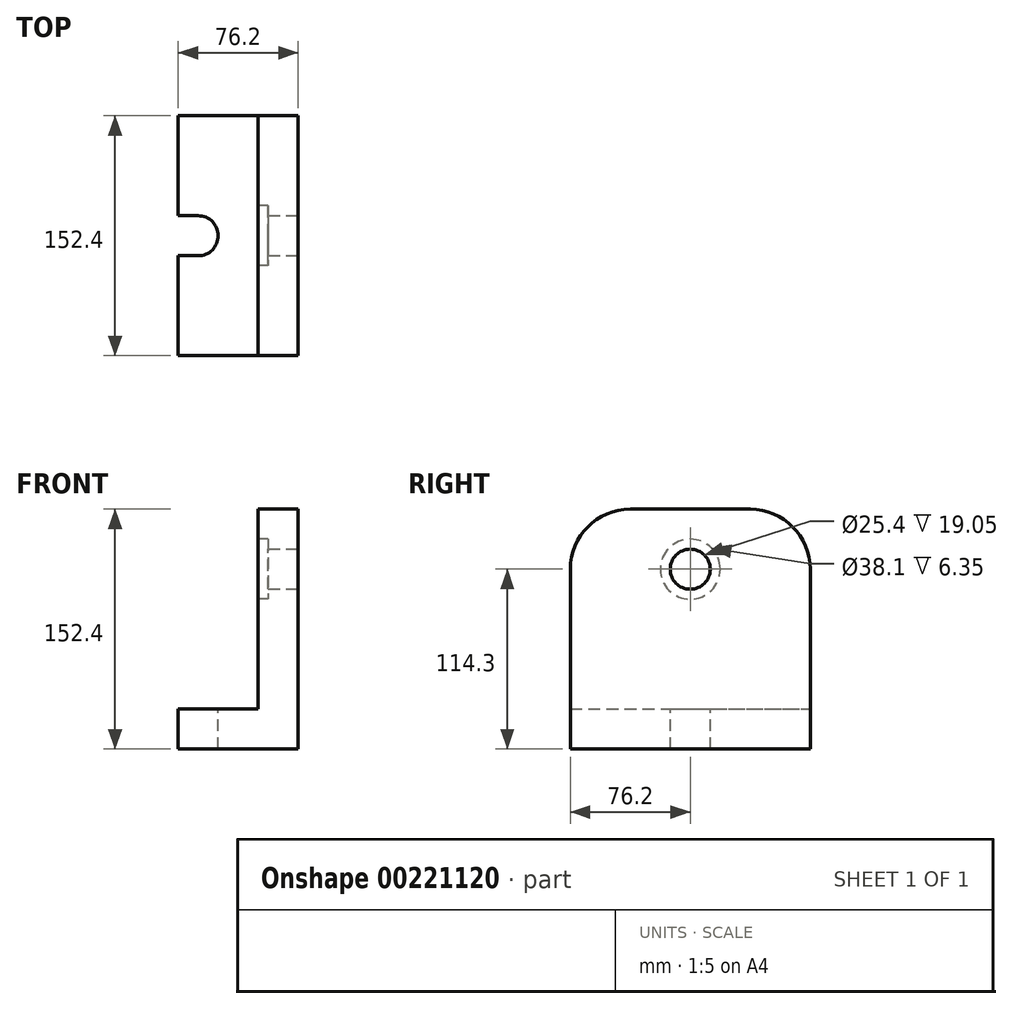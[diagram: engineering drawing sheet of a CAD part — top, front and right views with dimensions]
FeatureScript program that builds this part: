
annotation { "Feature Type Name" : "Feature", "Feature Type Description" : "" }
export const myFeature = defineFeature(function(context is Context, id is Id, definition is map)
    precondition{}
    {
        {
            var Q0;
            Q0=qCreatedBy(makeId("Front.planeOp"),FACE);
            var sketch = newSketch(context, id + "F0", { "sketchPlane" : qUnion([Q0])});
            skLineSegment(sketch, "E0", {"start": v(0, 0) * mm, "end": v(0, 152.4) * mm});
            skLineSegment(sketch, "E1", {"start": v(0, 152.4) * mm, "end": v(-25.4, 152.4) * mm});
            skLineSegment(sketch, "E2", {"start": v(-25.4, 152.4) * mm, "end": v(-25.4, 25.4) * mm});
            skLineSegment(sketch, "E3", {"start": v(-25.4, 25.4) * mm, "end": v(-76.2, 25.4) * mm});
            skLineSegment(sketch, "E4", {"start": v(-76.2, 25.4) * mm, "end": v(-76.2, 0) * mm});
            skLineSegment(sketch, "E5", {"start": v(-76.2, 0) * mm, "end": v(0, 0) * mm});
            skSolve(sketch);
        }
        {
            var Q0;
            Q0=makeQuery(id+"F0.imprint","IMPRINT",FACE,{"disambiguationData":[TD([[makeQuery(id+"F0.imprint","IMPRINT",EDGE,{"derivedFrom":sQuery(id+"F0.wireOp",EDGE,"E0")}),1.0]])]});
            extrude(context, id + "F1", {"entities" : qUnion([Q0]), "endBound" : BoundingType.SYMMETRIC, "depth" : 152.4 * mm});
        }
        {
            var Q0;
            Q0=makeQuery(id+"F1.opExtrude","SWEPT_FACE",FACE,{"disambiguationData":[OSD([sQuery(id+"F0.wireOp",EDGE,"E0")])]});
            var sketch = newSketch(context, id + "F2", { "sketchPlane" : qUnion([Q0])});
            skCircle(sketch, "E6", {"center": v(0, 114.3) * mm, "radius": 12.7 * mm});
            skSolve(sketch);
        }
        {
            var Q0;
            Q0=makeQuery(id+"F2.imprint","IMPRINT",FACE,{"disambiguationData":[TD([[makeQuery(id+"F2.imprint","IMPRINT",EDGE,{"derivedFrom":sQuery(id+"F2.wireOp",EDGE,"E6")}),1.0]])]});
            extrude(context, id + "F3", {"entities" : qUnion([Q0]), "operationType" : NewBodyOperationType.REMOVE, "endBound" : BoundingType.THROUGH_ALL, "oppositeDirection" : true, "depth" : 25.4 * mm});
        }
        {
            var Q0;
            Q0=makeQuery(id+"F1.opExtrude","SWEPT_FACE",FACE,{"disambiguationData":[OSD([sQuery(id+"F0.wireOp",EDGE,"E3")])]});
            var sketch = newSketch(context, id + "F4", { "sketchPlane" : qUnion([Q0])});
            skPoint(sketch, "E7.endSnap0", {"position": v(-76.2, 0) * mm});
            skPoint(sketch, "E8.positionSnap0", {"position": v(-50.8, 76.2) * mm});
            skLineSegment(sketch, "E9", {"start": v(-76.2, 0) * mm, "end": v(-63.5, 0) * mm});
            skLineSegment(sketch, "E10", {"start": v(-63.5, 12.7) * mm, "end": v(-76.2, 12.7) * mm});
            skLineSegment(sketch, "E11", {"start": v(-63.5, -12.7) * mm, "end": v(-76.2, -12.7) * mm});
            skArc(sketch, "E12", {"start": v(-63.5, -12.7) * mm, "mid": v(-50.8, 0) * mm, "end": v(-63.5, 12.7) * mm});
            skSolve(sketch);
        }
        {
            var Q0;
            {var subQ2=sQuery(id+"F4.wireOp",EDGE,"E10");Q0=makeQuery(id+"F4.imprint","IMPRINT",FACE,{"disambiguationData":[TD([[makeQuery(id+"F4.imprint","IMPRINT",EDGE,{"derivedFrom":subQ2}),1.0]])]});}
            extrude(context, id + "F5", {"entities" : qUnion([Q0]), "operationType" : NewBodyOperationType.REMOVE, "endBound" : BoundingType.THROUGH_ALL, "oppositeDirection" : true, "depth" : 25.4 * mm});
        }
        {
            var Q0;
            Q0=makeQuery(id+"F1.opExtrude","SWEPT_FACE",FACE,{"disambiguationData":[OSD([sQuery(id+"F0.wireOp",EDGE,"E2")])]});
            var sketch = newSketch(context, id + "F6", { "sketchPlane" : qUnion([Q0])});
            skCircle(sketch, "E13", {"center": v(0, 114.3) * mm, "radius": 19.05 * mm});
            skSolve(sketch);
        }
        {
            var Q0;
            Q0=makeQuery(id+"F6.imprint","IMPRINT",FACE,{"disambiguationData":[TD([[makeQuery(id+"F6.imprint","IMPRINT",EDGE,{"derivedFrom":sQuery(id+"F6.wireOp",EDGE,"E13")}),1.0]])]});
            var Q1;
            Q1=sQuery(id+"F6.wireOp",EDGE,"E13");
            extrude(context, id + "F7", {"entities" : qUnion([Q0]), "operationType" : NewBodyOperationType.REMOVE, "surfaceEntities" : qUnion([Q1]), "oppositeDirection" : true, "depth" : 6.35 * mm});
        }
        {
            var Q0;
            Q0=makeQuery(id+"F1.opExtrude","CAP_EDGE",EDGE,{"disambiguationData":[OSD([sQuery(id+"F0.wireOp",EDGE,"E1")])],"isStart":false});
            var Q1;
            Q1=makeQuery(id+"F1.opExtrude","CAP_EDGE",EDGE,{"disambiguationData":[OSD([sQuery(id+"F0.wireOp",EDGE,"E1")])],"isStart":true});
            fillet(context, id + "F8", {"entities" : qUnion([Q0, Q1]), "radius" : 38.1 * mm, "tangentPropagation" : true, "allowEdgeOverflow" : false});
        }
    });
